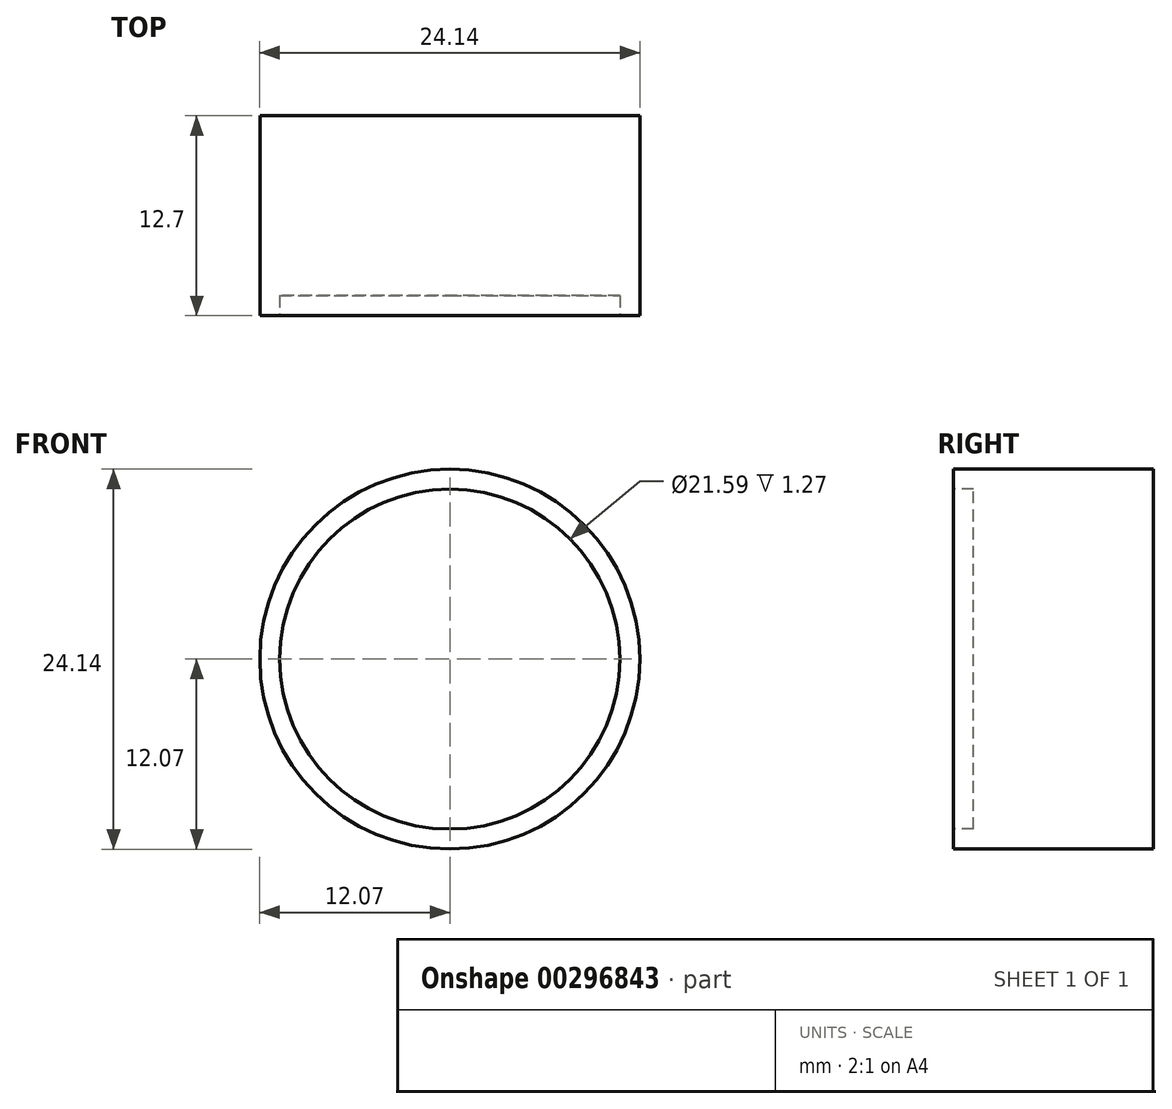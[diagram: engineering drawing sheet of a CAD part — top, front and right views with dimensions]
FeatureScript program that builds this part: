
annotation { "Feature Type Name" : "Feature", "Feature Type Description" : "" }
export const myFeature = defineFeature(function(context is Context, id is Id, definition is map)
    precondition{}
    {
        {
            var Q0;
            Q0=qCreatedBy(makeId("Front.planeOp"),FACE);
            var sketch = newSketch(context, id + "F0", { "sketchPlane" : qUnion([Q0])});
            skCircle(sketch, "E0", {"center": v(0, 0) * mm, "radius": 12.07 * mm});
            skSolve(sketch);
        }
        {
            var Q0;
            Q0=makeQuery(id+"F0.imprint","IMPRINT",FACE,{"disambiguationData":[TD([[makeQuery(id+"F0.imprint","IMPRINT",EDGE,{"derivedFrom":sQuery(id+"F0.wireOp",EDGE,"E0")}),1.0]])]});
            extrude(context, id + "F1", {"entities" : qUnion([Q0]), "depth" : 12.7 * mm});
        }
        {
            var Q0;
            Q0=qCreatedBy(makeId("Front.planeOp"),FACE);
            cPlane(context, id + "F2", {"entities" : qUnion([Q0]), "cplaneType" : CPlaneType.OFFSET, "offset" : 12.7 * mm, "width" : 152.4 * mm, "height" : 152.4 * mm});
        }
        {
            var Q0;
            Q0=qCreatedBy(id+"F2.planeOp",FACE);
            var sketch = newSketch(context, id + "F3", { "sketchPlane" : qUnion([Q0])});
            skCircle(sketch, "E1", {"center": v(0, 0) * mm, "radius": 10.8 * mm});
            skSolve(sketch);
        }
        {
            var Q0;
            Q0=makeQuery(id+"F3.imprint","IMPRINT",FACE,{"disambiguationData":[TD([[makeQuery(id+"F3.imprint","IMPRINT",EDGE,{"derivedFrom":sQuery(id+"F3.wireOp",EDGE,"E1")}),1.0]])]});
            extrude(context, id + "F4", {"entities" : qUnion([Q0]), "operationType" : NewBodyOperationType.REMOVE, "oppositeDirection" : true, "depth" : 1.27 * mm});
        }
    });
